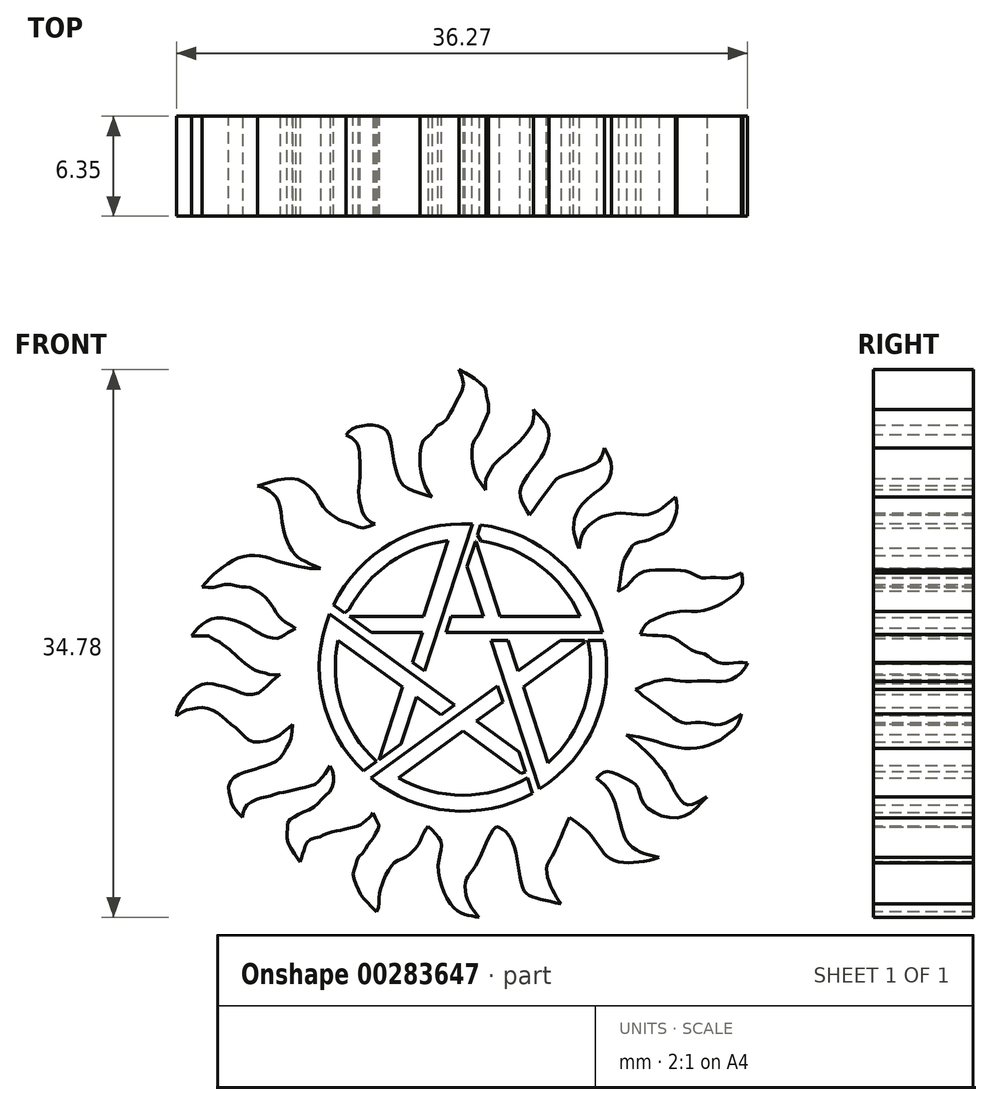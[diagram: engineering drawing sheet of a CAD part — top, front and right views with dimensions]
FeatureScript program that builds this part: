
annotation { "Feature Type Name" : "Feature", "Feature Type Description" : "" }
export const myFeature = defineFeature(function(context is Context, id is Id, definition is map)
    precondition{}
    {
        {
            var Q0;
            Q0=qCreatedBy(makeId("Front.planeOp"),FACE);
            var sketch = newSketch(context, id + "F0", { "sketchPlane" : qUnion([Q0])});
            skFitSpline(sketch, "E0", {"points": [v(17.15, 28.23) * mm, v(15.97, 28.6) * mm, v(15.2, 29.1) * mm, v(14.79, 30.17) * mm, v(14.58, 31.35) * mm, v(14.26, 32.42) * mm, v(13.56, 32.76) * mm, v(12.77, 32.76) * mm, v(12.04, 32.52) * mm, v(11.67, 32.16) * mm], "startDerivative": vector(-9.62, 2.67) * mm, "endDerivative": vector(-3.75, -4.8) * mm});
            skFitSpline(sketch, "E1", {"points": [v(13.5, 26.5) * mm, v(12.61, 26.26) * mm, v(12.04, 26.5) * mm, v(11.36, 26.7) * mm, v(10.88, 27.02) * mm, v(10.33, 27.44) * mm, v(9.94, 28.12) * mm, v(9.34, 28.9) * mm, v(8.4, 29.38) * mm, v(7.22, 29.28) * mm, v(6.04, 28.93) * mm], "startDerivative": vector(-9.25, -3.82) * mm, "endDerivative": vector(-9.76, -3.06) * mm});
            skFitSpline(sketch, "E2", {"points": [v(6.04, 28.93) * mm, v(6.82, 28.62) * mm, v(7.43, 27.83) * mm, v(7.6, 26.73) * mm, v(7.84, 25.63) * mm, v(8.32, 24.72) * mm, v(8.92, 24.22) * mm, v(10.05, 23.7) * mm], "startDerivative": vector(6.27, -1.71) * mm, "endDerivative": vector(7.72, -3.28) * mm});
            skFitSpline(sketch, "E3", {"points": [v(10.05, 23.7) * mm, v(9.33, 23.7) * mm, v(8.46, 23.87) * mm, v(7.52, 24.1) * mm, v(6.81, 24.34) * mm, v(6.09, 24.5) * mm, v(5.34, 24.49) * mm, v(4.5, 24.2) * mm, v(3.76, 23.7) * mm, v(3.13, 23.2) * mm, v(2.53, 22.51) * mm], "startDerivative": vector(-7.56, -0.4) * mm, "endDerivative": vector(-5.62, -6.95) * mm});
            skFitSpline(sketch, "E4", {"points": [v(2.53, 22.51) * mm, v(3.38, 22.51) * mm, v(4.2, 22.68) * mm, v(5.07, 22.51) * mm, v(5.46, 22.51) * mm, v(5.96, 22.28) * mm, v(6.44, 21.97) * mm, v(6.8, 21.57) * mm, v(7.06, 21.18) * mm, v(7.42, 20.62) * mm, v(7.75, 20.33) * mm, v(8.08, 20.12) * mm, v(8.48, 19.89) * mm], "startDerivative": vector(8.57, -0.74) * mm, "endDerivative": vector(5.45, -3.12) * mm});
            skFitSpline(sketch, "E5", {"points": [v(1.87, 19.4) * mm, v(2.26, 19.4) * mm, v(2.53, 19.4) * mm, v(2.98, 19.4) * mm, v(3.2, 19.22) * mm, v(3.6, 19.03) * mm, v(3.88, 18.82) * mm, v(4.22, 18.6) * mm, v(4.4, 18.41) * mm, v(4.69, 18.18) * mm, v(4.97, 17.88) * mm, v(5.3, 17.63) * mm, v(5.63, 17.4) * mm, v(5.94, 17.2) * mm, v(6.42, 17.07) * mm, v(6.84, 16.95) * mm, v(7.48, 16.95) * mm], "startDerivative": vector(6.84, 0.07) * mm, "endDerivative": vector(8.68, 0.55) * mm});
            skFitSpline(sketch, "E6", {"points": [v(7.48, 16.95) * mm, v(6.84, 16.42) * mm, v(6.19, 15.83) * mm, v(5.3, 15.7) * mm, v(4.44, 16.02) * mm, v(3.55, 16.28) * mm, v(2.76, 16.37) * mm, v(1.87, 15.93) * mm, v(1.43, 15.46) * mm, v(1, 14.76) * mm, v(0.91, 14.31) * mm], "startDerivative": vector(-6.53, -4.97) * mm, "endDerivative": vector(-0.56, -5.57) * mm});
            skFitSpline(sketch, "E7", {"points": [v(0.91, 14.31) * mm, v(1.5, 14.69) * mm, v(2.08, 14.78) * mm, v(2.53, 14.85) * mm, v(3.15, 14.69) * mm, v(3.6, 14.45) * mm, v(4.11, 13.99) * mm, v(4.67, 13.54) * mm, v(5.16, 13.08) * mm, v(5.63, 12.73) * mm, v(6.3, 12.68) * mm, v(7.25, 12.98) * mm, v(7.82, 13.4) * mm, v(8.27, 13.78) * mm], "startDerivative": vector(7.07, 5.7) * mm, "endDerivative": vector(6.04, 5.04) * mm});
            skFitSpline(sketch, "E8", {"points": [v(8.27, 13.78) * mm, v(8.14, 12.75) * mm, v(7.85, 12.23) * mm, v(7.4, 11.56) * mm, v(6.66, 11.2) * mm, v(6, 10.97) * mm, v(5.27, 10.75) * mm, v(4.66, 10.47) * mm, v(4.24, 9.93) * mm, v(4.3, 9.19) * mm, v(4.5, 8.54) * mm, v(5.1, 7.88) * mm], "startDerivative": vector(0.15, -10.52) * mm, "endDerivative": vector(7.05, -6.62) * mm});
            skFitSpline(sketch, "E9", {"points": [v(5.1, 7.88) * mm, v(5.27, 8.52) * mm, v(6.04, 9.04) * mm, v(6.84, 9.24) * mm, v(7.48, 9.43) * mm, v(8.17, 9.56) * mm, v(8.76, 9.73) * mm, v(9.64, 9.95) * mm, v(10.22, 10.5) * mm, v(10.67, 11.14) * mm], "startDerivative": vector(0.87, 6.46) * mm, "endDerivative": vector(3.82, 5.75) * mm});
            skFitSpline(sketch, "E10", {"points": [v(10.67, 11.14) * mm, v(10.87, 10.55) * mm, v(10.81, 9.86) * mm, v(10.52, 9.4) * mm, v(10.05, 8.96) * mm, v(9.64, 8.53) * mm, v(8.95, 8.21) * mm, v(8.48, 7.96) * mm, v(8.03, 7.66) * mm, v(7.95, 7.17) * mm, v(7.9, 6.72) * mm, v(8.05, 6.15) * mm, v(8.48, 5.42) * mm, v(8.75, 5.03) * mm], "startDerivative": vector(3.3, -7.18) * mm, "endDerivative": vector(3.66, -5.15) * mm});
            skFitSpline(sketch, "E11", {"points": [v(8.75, 5.03) * mm, v(8.9, 5.54) * mm, v(9.07, 6) * mm, v(9.38, 6.45) * mm, v(10.05, 6.66) * mm, v(10.52, 6.88) * mm, v(11.15, 7.01) * mm, v(11.58, 7.11) * mm, v(12.09, 7.23) * mm, v(12.59, 7.39) * mm, v(12.87, 7.64) * mm, v(13.2, 7.9) * mm, v(13.38, 8.17) * mm], "startDerivative": vector(1.85, 6.06) * mm, "endDerivative": vector(2.12, 4.3) * mm});
            skFitSpline(sketch, "E12", {"points": [v(13.38, 8.17) * mm, v(13.62, 7.66) * mm, v(13.76, 7.29) * mm, v(13.58, 6.92) * mm, v(13.38, 6.54) * mm, v(13.03, 6.11) * mm, v(12.74, 5.6) * mm, v(12.4, 5.27) * mm, v(12.3, 4.86) * mm, v(12.13, 4.3) * mm, v(12.29, 3.66) * mm, v(12.59, 3) * mm, v(12.91, 2.6) * mm, v(13.62, 1.87) * mm], "startDerivative": vector(2.94, -6.83) * mm, "endDerivative": vector(7.48, -7.57) * mm});
            skFitSpline(sketch, "E13", {"points": [v(13.62, 1.87) * mm, v(13.78, 2.4) * mm, v(13.78, 2.97) * mm, v(13.92, 3.46) * mm, v(14.07, 3.97) * mm, v(14.46, 4.66) * mm, v(14.79, 5.03) * mm, v(15.25, 5.25) * mm, v(15.64, 5.46) * mm, v(15.96, 5.78) * mm, v(16.3, 6.2) * mm, v(16.5, 6.68) * mm, v(16.7, 7.05) * mm, v(16.88, 7.3) * mm], "startDerivative": vector(2.61, 6.45) * mm, "endDerivative": vector(2.94, 4.04) * mm});
            skFitSpline(sketch, "E14", {"points": [v(16.88, 7.3) * mm, v(17.73, 6.2) * mm, v(17.52, 4.72) * mm, v(18.42, 2.22) * mm, v(19.32, 1.7) * mm, v(20.12, 1.53) * mm], "startDerivative": vector(5.9, -5.45) * mm, "endDerivative": vector(5.26, -0.9) * mm});
            skFitSpline(sketch, "E15", {"points": [v(20.12, 1.53) * mm, v(19.43, 2.54) * mm, v(19.27, 3.87) * mm, v(19.86, 4.72) * mm, v(21.13, 7.23) * mm, v(21.4, 7.23) * mm], "startDerivative": vector(-3.86, 4.43) * mm, "endDerivative": vector(2.63, -1.28) * mm});
            skFitSpline(sketch, "E16", {"points": [v(21.4, 7.23) * mm, v(22.09, 6.64) * mm, v(22.62, 4.72) * mm, v(23.05, 3.13) * mm, v(23.74, 2.75) * mm, v(25.32, 2.38) * mm], "startDerivative": vector(4.6, -2.71) * mm, "endDerivative": vector(7.91, -1.75) * mm});
            skFitSpline(sketch, "E17", {"points": [v(25.32, 2.38) * mm, v(24.69, 3.45) * mm, v(24.42, 4.72) * mm, v(24.8, 5.47) * mm, v(25.32, 6.64) * mm, v(25.86, 7.86) * mm], "startDerivative": vector(-3.35, 4.82) * mm, "endDerivative": vector(2.53, 5.69) * mm});
            skFitSpline(sketch, "E18", {"points": [v(27.57, 10.36) * mm, v(28.26, 10.78) * mm, v(29.37, 10.36) * mm, v(30.17, 9.83) * mm, v(30.61, 8.7) * mm, v(32.78, 7.86) * mm, v(34.59, 9.19) * mm], "startDerivative": vector(4.98, 4.83) * mm, "endDerivative": vector(7.51, 8.7) * mm});
            skFitSpline(sketch, "E19", {"points": [v(34.59, 9.19) * mm, v(33.26, 8.7) * mm, v(32.4, 9.83) * mm, v(31.77, 10.89) * mm, v(30.61, 12.17) * mm, v(29.47, 13.12) * mm], "startDerivative": vector(-7.28, -4.6) * mm, "endDerivative": vector(-5.58, 4.37) * mm});
            skFitSpline(sketch, "E20", {"points": [v(36.8, 14.45) * mm, v(35.36, 13.76) * mm, v(34.14, 13.92) * mm, v(33.13, 13.87) * mm, v(32.12, 14.45) * mm, v(31, 15.25) * mm, v(30.05, 16) * mm], "startDerivative": vector(-7.68, -5.2) * mm, "endDerivative": vector(-5.69, 4.57) * mm});
            skFitSpline(sketch, "E21", {"points": [v(30.05, 16) * mm, v(31, 16.42) * mm, v(32.12, 16.63) * mm, v(33.13, 16.5) * mm, v(34.65, 16.55) * mm, v(35.87, 16.55) * mm, v(36.8, 17.1) * mm, v(37.18, 17.69) * mm], "startDerivative": vector(6.54, 3.28) * mm, "endDerivative": vector(1.86, 5.4) * mm});
            skFitSpline(sketch, "E22", {"points": [v(37.18, 17.69) * mm, v(36.38, 17.69) * mm, v(35.36, 17.69) * mm, v(34.44, 18.24) * mm, v(33.72, 18.45) * mm, v(32.8, 19.08) * mm, v(32.12, 19.38) * mm, v(31.6, 19.42) * mm, v(30.36, 19.5) * mm], "startDerivative": vector(-6.6, 0.31) * mm, "endDerivative": vector(-8.88, 0.77) * mm});
            skFitSpline(sketch, "E23", {"points": [v(30.36, 19.5) * mm, v(30.8, 20.22) * mm, v(31.57, 20.6) * mm, v(32.12, 20.81) * mm, v(33.13, 20.98) * mm, v(34.14, 20.98) * mm, v(35.36, 21.36) * mm, v(36.08, 21.83) * mm, v(36.8, 22.54) * mm, v(36.8, 23.4) * mm], "startDerivative": vector(3.21, 7.48) * mm, "endDerivative": vector(-1.74, 8.03) * mm});
            skFitSpline(sketch, "E24", {"points": [v(36.8, 23.4) * mm, v(36, 23.1) * mm, v(34.87, 23.1) * mm, v(34.23, 23.1) * mm, v(33.63, 23.4) * mm, v(32.87, 23.57) * mm, v(31.48, 23.58) * mm, v(30.36, 23.4) * mm, v(29.47, 22.54) * mm], "startDerivative": vector(-6.79, -2.96) * mm, "endDerivative": vector(-6.48, -5.97) * mm});
            skFitSpline(sketch, "E25", {"points": [v(29.47, 22.54) * mm, v(28.97, 22.23) * mm], "startDerivative": vector(-0.55, -0.38) * mm, "endDerivative": vector(-0.55, -0.38) * mm});
            skFitSpline(sketch, "E26", {"points": [v(28.97, 22.23) * mm, v(29.15, 23.4) * mm, v(29.29, 24.11) * mm, v(29.75, 24.94) * mm, v(30.05, 25.28) * mm, v(30.8, 25.47) * mm, v(31.56, 25.8) * mm, v(32.12, 26.1) * mm, v(32.69, 27.5) * mm, v(32.6, 28.21) * mm], "startDerivative": vector(1.16, 9.18) * mm, "endDerivative": vector(-1.46, 5.94) * mm});
            skFitSpline(sketch, "E27", {"points": [v(32.6, 28.21) * mm, v(31.59, 27.42) * mm, v(30.61, 27.08) * mm, v(29.29, 27.2) * mm, v(28.35, 27.08) * mm, v(27.64, 26.82) * mm, v(26.74, 25.96) * mm, v(26.47, 24.94) * mm], "startDerivative": vector(-6.51, -5.56) * mm, "endDerivative": vector(-0.83, -7.39) * mm});
            skFitSpline(sketch, "E28", {"points": [v(20.53, 28.68) * mm, v(19.96, 29.47) * mm, v(19.8, 29.98) * mm, v(19.7, 30.5) * mm, v(19.66, 31.16) * mm, v(19.8, 31.78) * mm, v(20.12, 32.22) * mm, v(20.42, 32.96) * mm, v(20.73, 33.8) * mm, v(20.56, 34.86) * mm, v(20.56, 35.05) * mm, v(19.97, 35.65) * mm, v(19.56, 35.92) * mm, v(18.83, 36.31) * mm], "startDerivative": vector(-6.12, 9.35) * mm, "endDerivative": vector(-10.75, 4.06) * mm});
            skFitSpline(sketch, "E29", {"points": [v(18.83, 36.31) * mm, v(19.14, 35.38) * mm, v(18.83, 34.59) * mm, v(18.54, 34.02) * mm, v(18.25, 33.48) * mm, v(17.9, 33) * mm, v(17.43, 32.71) * mm, v(17.1, 32.27) * mm, v(16.7, 31.95) * mm, v(16.5, 31.66) * mm, v(16.38, 30.87) * mm, v(16.38, 30.3) * mm, v(16.44, 29.7) * mm, v(16.73, 28.83) * mm, v(17.15, 28.23) * mm], "startDerivative": vector(5.48, -10.72) * mm, "endDerivative": vector(5.89, -7.33) * mm});
            skFitSpline(sketch, "E30", {"points": [v(27.57, 10.36) * mm, v(28.32, 9.66) * mm, v(28.8, 8.62) * mm, v(29.08, 7.58) * mm, v(29.31, 6.73) * mm, v(29.74, 6.1) * mm, v(30.38, 5.67) * mm, v(30.87, 5.5) * mm, v(31.56, 5.34) * mm], "startDerivative": vector(6, -4.55) * mm, "endDerivative": vector(6.34, -1.49) * mm});
            skFitSpline(sketch, "E31", {"points": [v(25.86, 7.86) * mm, v(26.36, 7.51) * mm, v(27.1, 6.9) * mm, v(27.4, 6.52) * mm, v(27.8, 5.95) * mm, v(28.09, 5.57) * mm, v(28.41, 5.28) * mm, v(29.08, 5.03) * mm, v(29.88, 5) * mm, v(30.75, 5.11) * mm, v(31.56, 5.34) * mm], "startDerivative": vector(4.9, -3.21) * mm, "endDerivative": vector(7.15, 2.26) * mm});
            skFitSpline(sketch, "E32", {"points": [v(29.47, 13.12) * mm, v(30.9, 12.83) * mm, v(32.06, 12.48) * mm, v(33.33, 12.25) * mm, v(34.77, 12.48) * mm, v(35.9, 13.12) * mm, v(36.57, 13.79) * mm, v(36.8, 14.45) * mm], "startDerivative": vector(9.32, -1.7) * mm, "endDerivative": vector(1.44, 6.2) * mm});
            skFitSpline(sketch, "E33", {"points": [v(26.47, 24.94) * mm, v(26.17, 25.89) * mm, v(26.15, 26.62) * mm, v(26.47, 27.5) * mm, v(27.31, 28.34) * mm, v(28.04, 28.94) * mm, v(28.46, 29.56) * mm, v(28.5, 30.44) * mm, v(28.25, 31.02) * mm, v(28.1, 31.34) * mm], "startDerivative": vector(-2.98, 7.91) * mm, "endDerivative": vector(-1.83, 4.1) * mm});
            skFitSpline(sketch, "E34", {"points": [v(28.1, 31.34) * mm, v(27.78, 30.6) * mm, v(27.26, 30.22) * mm, v(26.47, 29.9) * mm, v(25.64, 29.64) * mm, v(25.03, 29.35) * mm, v(24.54, 28.72) * mm, v(24.01, 28.02) * mm, v(23.68, 27.54) * mm, v(23.32, 27.08) * mm], "startDerivative": vector(-2.18, -7.16) * mm, "endDerivative": vector(-3.77, -4.58) * mm});
            skFitSpline(sketch, "E35", {"points": [v(23.32, 27.08) * mm, v(22.98, 27.69) * mm, v(22.72, 28.38) * mm, v(22.85, 29) * mm, v(23.19, 29.56) * mm, v(23.62, 30.12) * mm, v(24.16, 30.93) * mm, v(24.52, 31.87) * mm, v(24.43, 32.77) * mm, v(23.8, 33.54) * mm, v(23.58, 33.78) * mm], "startDerivative": vector(-3.49, 6.07) * mm, "endDerivative": vector(-2.78, 3.13) * mm});
            skFitSpline(sketch, "E36", {"points": [v(23.58, 33.78) * mm, v(23.56, 33.07) * mm, v(23.32, 32.54) * mm, v(22.89, 31.98) * mm, v(21.91, 31.06) * mm, v(21.2, 30.42) * mm, v(20.79, 29.86) * mm, v(20.54, 29.26) * mm, v(20.53, 28.68) * mm], "startDerivative": vector(0.37, -6.16) * mm, "endDerivative": vector(0.27, -5.3) * mm});
            skFitSpline(sketch, "E37", {"points": [v(11.67, 32.16) * mm, v(12, 32) * mm, v(12.24, 31.8) * mm, v(12.46, 31.44) * mm, v(12.53, 30.93) * mm, v(12.56, 30.2) * mm, v(12.54, 29.28) * mm, v(12.48, 28.5) * mm, v(12.6, 27.67) * mm, v(12.9, 26.93) * mm, v(13.5, 26.5) * mm], "startDerivative": vector(4.57, -2.09) * mm, "endDerivative": vector(6.19, -3.34) * mm});
            skFitSpline(sketch, "E38", {"points": [v(8.48, 19.89) * mm, v(7.86, 19.53) * mm, v(7.33, 19.26) * mm, v(6.5, 19.4) * mm, v(5.66, 19.89) * mm, v(4.74, 20.33) * mm, v(3.5, 20.56) * mm, v(2.51, 20.13) * mm, v(1.87, 19.4) * mm], "startDerivative": vector(-5.78, -3.24) * mm, "endDerivative": vector(-4.53, -6.1) * mm});
            skSolve(sketch);
        }
        {
            var Q0;
            Q0 = qSketchRegion(id + "F0", true);
            extrude(context, id + "F1", {"entities" : qUnion([Q0]), "oppositeDirection" : true, "depth" : 6.35 * mm});
        }
        {
            var Q0;
            {var subQ11=sQuery(id+"F0.wireOp",EDGE,"E0");Q0=makeQuery(id+"F0.imprint","IMPRINT",FACE,{"disambiguationData":[TD([[makeQuery(id+"F0.imprint","IMPRINT",EDGE,{"derivedFrom":subQ11}),1.0]])]});}
            var sketch = newSketch(context, id + "F2", { "sketchPlane" : qUnion([Q0])});
            skLineSegment(sketch, "E39.0", {"start": v(21.3, 16.22) * mm, "end": v(19.1, 14.62) * mm});
            skLineSegment(sketch, "E39.1", {"start": v(18.56, 15.02) * mm, "end": v(16.47, 16.54) * mm});
            skLineSegment(sketch, "E39.2", {"start": v(16.67, 17.17) * mm, "end": v(17.47, 19.63) * mm});
            skLineSegment(sketch, "E39.3", {"start": v(18, 19.63) * mm, "end": v(20.73, 19.63) * mm});
            skLineSegment(sketch, "E39.4", {"start": v(20.9, 19.13) * mm, "end": v(21.73, 16.54) * mm});
            skLineSegment(sketch, "E40", {"start": v(16.67, 17.17) * mm, "end": v(19.7, 26.5) * mm});
            skLineSegment(sketch, "E41", {"start": v(16.14, 15.52) * mm, "end": v(15.17, 12.56) * mm});
            skLineSegment(sketch, "E42", {"start": v(19.96, 14) * mm, "end": v(22.66, 12.04) * mm});
            skLineSegment(sketch, "E43", {"start": v(20.4, 20.65) * mm, "end": v(19.37, 23.82) * mm});
            skLineSegment(sketch, "E44", {"start": v(21.73, 16.54) * mm, "end": v(23.96, 9.67) * mm});
            skArc(sketch, "E45", {"start": v(19.7, 26.5) * mm, "mid": v(14.51, 25.28) * mm, "end": v(10.89, 21.37) * mm});
            skArc(sketch, "E46", {"start": v(18.16, 25.45) * mm, "mid": v(14.47, 24.05) * mm, "end": v(11.87, 21.08) * mm});
            skLineSegment(sketch, "E47", {"start": v(19.1, 14.62) * mm, "end": v(13.26, 10.38) * mm});
            skLineSegment(sketch, "E48", {"start": v(13.26, 10.38) * mm, "end": v(21.3, 16.22) * mm});
            skLineSegment(sketch, "E49", {"start": v(22.6, 17.17) * mm, "end": v(25.3, 19.13) * mm});
            skLineSegment(sketch, "E50", {"start": v(20.73, 19.63) * mm, "end": v(27.95, 19.63) * mm});
            skLineSegment(sketch, "E51", {"start": v(16.52, 19.63) * mm, "end": v(13.28, 19.63) * mm});
            skLineSegment(sketch, "E52", {"start": v(16.47, 16.54) * mm, "end": v(10.62, 20.78) * mm});
            skLineSegment(sketch, "E53", {"start": v(15.17, 12.56) * mm, "end": v(13.77, 11.54) * mm});
            skLineSegment(sketch, "E54", {"start": v(11.18, 19.13) * mm, "end": v(15.27, 16.15) * mm});
            skLineSegment(sketch, "E55", {"start": v(15.27, 16.15) * mm, "end": v(13.77, 11.54) * mm});
            skLineSegment(sketch, "E56", {"start": v(16.14, 15.52) * mm, "end": v(17.7, 14.39) * mm});
            skLineSegment(sketch, "E57", {"start": v(23.07, 10.77) * mm, "end": v(22.66, 12.04) * mm});
            skLineSegment(sketch, "E58", {"start": v(17.7, 14.39) * mm, "end": v(18.56, 15.02) * mm});
            skLineSegment(sketch, "E59", {"start": v(15, 10.4) * mm, "end": v(19.1, 13.37) * mm});
            skLineSegment(sketch, "E60", {"start": v(21.63, 15.2) * mm, "end": v(21.3, 16.22) * mm});
            skLineSegment(sketch, "E61", {"start": v(24.5, 11.33) * mm, "end": v(22.93, 16.15) * mm});
            skLineSegment(sketch, "E62", {"start": v(28.06, 19.13) * mm, "end": v(27.05, 19.13) * mm});
            skLineSegment(sketch, "E63", {"start": v(11.88, 20.65) * mm, "end": v(16.6, 20.65) * mm});
            skLineSegment(sketch, "E64", {"start": v(18, 19.63) * mm, "end": v(18.34, 20.65) * mm});
            skLineSegment(sketch, "E65", {"start": v(11.58, 20.87) * mm, "end": v(10.89, 21.37) * mm});
            skLineSegment(sketch, "E66", {"start": v(10.89, 21.37) * mm, "end": v(11.58, 20.87) * mm});
            skLineSegment(sketch, "E67", {"start": v(11.88, 20.65) * mm, "end": v(13.28, 19.63) * mm});
            skLineSegment(sketch, "E68.trimOffspring", {"start": v(19.37, 23.82) * mm, "end": v(19.88, 25.4) * mm});
            skLineSegment(sketch, "E69.trimOffspring", {"start": v(18.34, 20.65) * mm, "end": v(20.4, 20.65) * mm});
            skLineSegment(sketch, "E70.trimOffspring", {"start": v(15.9, 17.73) * mm, "end": v(16.67, 17.17) * mm});
            skArc(sketch, "E71.trimOffspring", {"start": v(11.18, 19.13) * mm, "mid": v(11.37, 14.95) * mm, "end": v(13.61, 11.42) * mm});
            skArc(sketch, "E72.trimOffspring", {"start": v(10.62, 20.78) * mm, "mid": v(10.18, 15.47) * mm, "end": v(12.77, 10.81) * mm});
            skLineSegment(sketch, "E73.trimOffspring", {"start": v(21.47, 20.65) * mm, "end": v(19.92, 25.4) * mm});
            skLineSegment(sketch, "E74.trimOffspring", {"start": v(16.6, 20.65) * mm, "end": v(18.16, 25.45) * mm});
            skLineSegment(sketch, "E75.trimOffspring", {"start": v(21.47, 20.65) * mm, "end": v(26.53, 20.65) * mm});
            skArc(sketch, "E76.trimOffspring", {"start": v(26.53, 20.65) * mm, "mid": v(24, 23.86) * mm, "end": v(20.23, 25.43) * mm});
            skLineSegment(sketch, "E77.trimOffspring", {"start": v(15.9, 17.73) * mm, "end": v(16.52, 19.63) * mm});
            skLineSegment(sketch, "E78.trimOffspring", {"start": v(21.96, 19.13) * mm, "end": v(20.9, 19.13) * mm});
            skArc(sketch, "E79.trimOffspring", {"start": v(27.95, 19.63) * mm, "mid": v(25.14, 24.24) * mm, "end": v(20.22, 26.45) * mm});
            skLineSegment(sketch, "E80.trimOffspring", {"start": v(22.6, 17.17) * mm, "end": v(21.96, 19.13) * mm});
            skLineSegment(sketch, "E81.trimOffspring", {"start": v(22.93, 16.15) * mm, "end": v(26.86, 19) * mm});
            skLineSegment(sketch, "E82.trimOffspring", {"start": v(19.1, 13.37) * mm, "end": v(22.8, 10.68) * mm});
            skLineSegment(sketch, "E83.trimOffspring", {"start": v(19.96, 14) * mm, "end": v(21.63, 15.2) * mm});
            skArc(sketch, "E84.trimOffspring", {"start": v(15, 10.4) * mm, "mid": v(19.1, 9.28) * mm, "end": v(23.2, 10.4) * mm});
            skArc(sketch, "E85.trimOffspring", {"start": v(13.26, 10.38) * mm, "mid": v(18.24, 8.3) * mm, "end": v(23.52, 9.4) * mm});
            skArc(sketch, "E86.trimOffspring", {"start": v(24.5, 11.33) * mm, "mid": v(26.8, 14.86) * mm, "end": v(27.03, 19.07) * mm});
            skLineSegment(sketch, "E87", {"start": v(22.66, 12.04) * mm, "end": v(23.07, 10.77) * mm});
            skArc(sketch, "E88.trimOffspring", {"start": v(23.96, 9.67) * mm, "mid": v(27.47, 13.76) * mm, "end": v(28.06, 19.13) * mm});
            skLineSegment(sketch, "E89.trimOffspring", {"start": v(13.61, 11.42) * mm, "end": v(12.77, 10.81) * mm});
            skLineSegment(sketch, "E90", {"start": v(22.8, 10.68) * mm, "end": v(23.07, 10.77) * mm});
            skLineSegment(sketch, "E91.trimOffspring", {"start": v(23.2, 10.4) * mm, "end": v(23.52, 9.4) * mm});
            skLineSegment(sketch, "E92", {"start": v(26.86, 19) * mm, "end": v(26.82, 19.13) * mm});
            skLineSegment(sketch, "E93", {"start": v(27.03, 19.07) * mm, "end": v(27.05, 19.13) * mm});
            skLineSegment(sketch, "E94.trimOffspring", {"start": v(26.82, 19.13) * mm, "end": v(25.3, 19.13) * mm});
            skLineSegment(sketch, "E95", {"start": v(19.92, 25.4) * mm, "end": v(19.88, 25.4) * mm});
            skLineSegment(sketch, "E96", {"start": v(20.23, 25.43) * mm, "end": v(20.02, 25.82) * mm});
            skLineSegment(sketch, "E97.trimOffspring", {"start": v(20.02, 25.82) * mm, "end": v(20.22, 26.45) * mm});
            skLineSegment(sketch, "E98", {"start": v(11.87, 21.08) * mm, "end": v(11.58, 20.87) * mm});
            skSolve(sketch);
        }
        {
            var Q0;
            {var subQ2=sQuery(id+"F2.wireOp",EDGE,"E45");Q0=makeQuery(id+"F2.imprint","IMPRINT",FACE,{"disambiguationData":[TD([[makeQuery(id+"F2.imprint","IMPRINT",EDGE,{"derivedFrom":subQ2}),1.0]])]});}
            var Q1;
            Q1=makeQuery(id+"F2.imprint","IMPRINT",FACE,{"disambiguationData":[TD([[makeQuery(id+"F2.imprint","IMPRINT",EDGE,{"derivedFrom":sQuery(id+"F2.wireOp",EDGE,"E39.1")}),1.0]])]});
            var Q2;
            Q2=makeQuery(id+"F2.imprint","IMPRINT",FACE,{"disambiguationData":[TD([[makeQuery(id+"F2.imprint","IMPRINT",EDGE,{"derivedFrom":sQuery(id+"F2.wireOp",EDGE,"E42")}),-1.0]])]});
            var Q3;
            Q3=makeQuery(id+"F2.imprint","IMPRINT",FACE,{"disambiguationData":[TD([[makeQuery(id+"F2.imprint","IMPRINT",EDGE,{"derivedFrom":sQuery(id+"F2.wireOp",EDGE,"E39.4")}),1.0]])]});
            var Q4;
            Q4=makeQuery(id+"F2.imprint","IMPRINT",FACE,{"disambiguationData":[TD([[makeQuery(id+"F2.imprint","IMPRINT",EDGE,{"derivedFrom":sQuery(id+"F2.wireOp",EDGE,"E39.3")}),1.0]])]});
            extrude(context, id + "F3", {"entities" : qUnion([Q0, Q1, Q2, Q3, Q4]), "operationType" : NewBodyOperationType.REMOVE, "oppositeDirection" : true, "depth" : .125 / 50.8 * mm});
        }
    });
